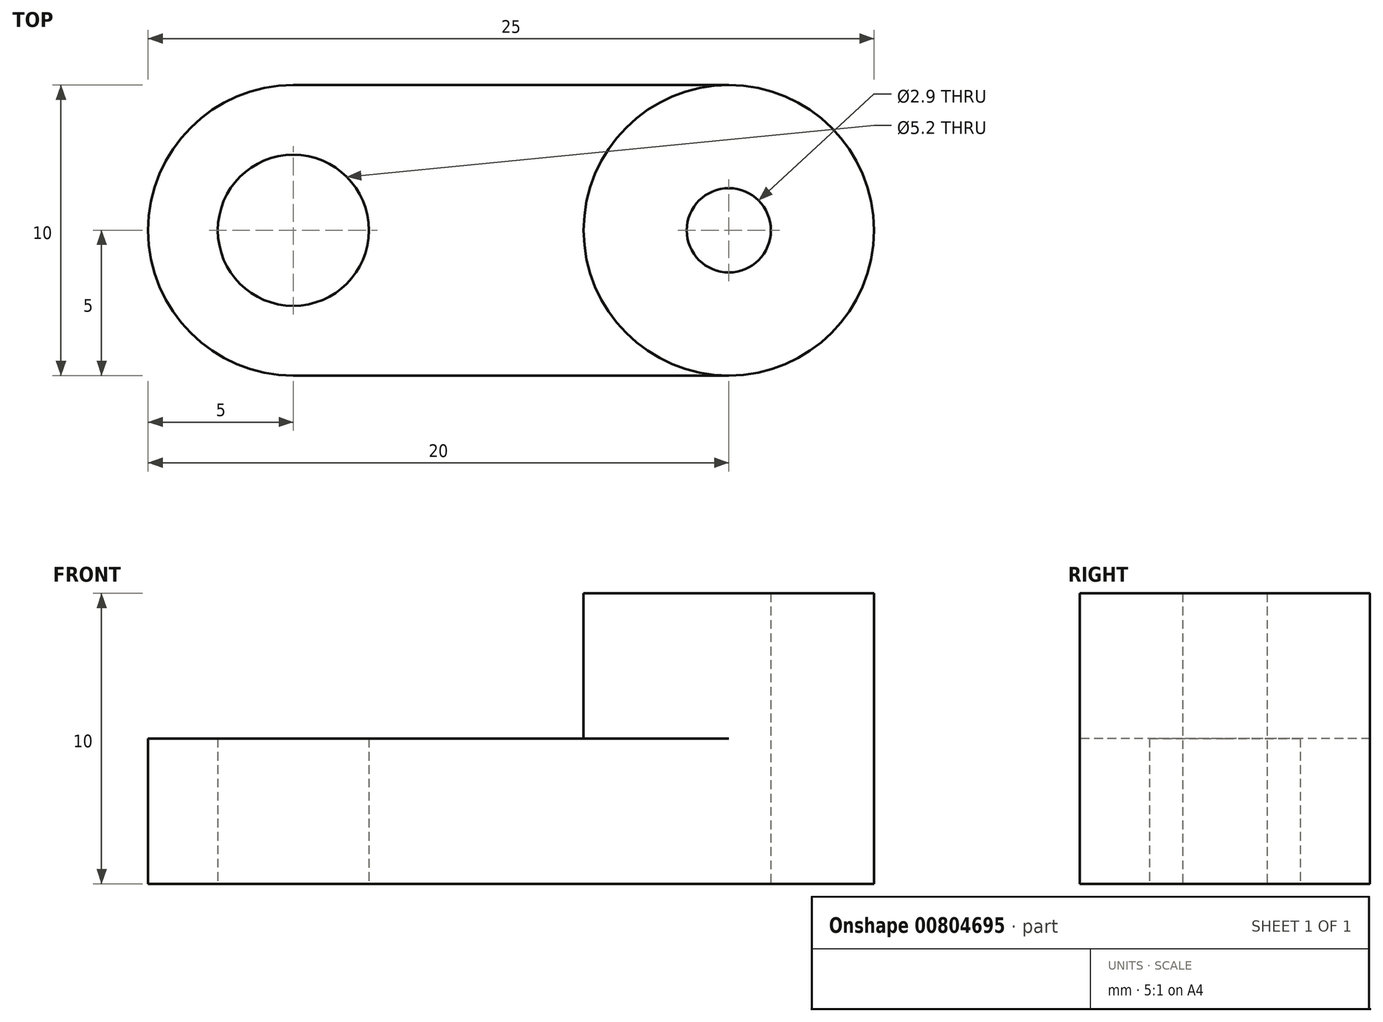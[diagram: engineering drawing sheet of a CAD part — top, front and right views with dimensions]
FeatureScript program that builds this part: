
annotation { "Feature Type Name" : "Feature", "Feature Type Description" : "" }
export const myFeature = defineFeature(function(context is Context, id is Id, definition is map)
    precondition{}
    {
        {
            var Q0;
            Q0=qCreatedBy(makeId("Top.planeOp"),FACE);
            var sketch = newSketch(context, id + "F0", { "sketchPlane" : qUnion([Q0])});
            skLineSegment(sketch, "E0", {"start": v(0, 0) * mm, "end": v(15, 0) * mm});
            skArc(sketch, "E1.0.startCap", {"start": v(0, -5) * mm, "mid": v(-5, 0) * mm, "end": v(0, 5) * mm});
            skArc(sketch, "E1.0.endCap", {"start": v(15, 5) * mm, "mid": v(20, 0) * mm, "end": v(15, -5) * mm});
            skLineSegment(sketch, "E1.0.left", {"start": v(0, 5) * mm, "end": v(15, 5) * mm});
            skLineSegment(sketch, "E1.0.right", {"start": v(0, -5) * mm, "end": v(15, -5) * mm});
            skCircle(sketch, "E2", {"center": v(0, 0) * mm, "radius": 2.6 * mm});
            skCircle(sketch, "E3", {"center": v(15, 0) * mm, "radius": 1.45 * mm});
            skSolve(sketch);
        }
        {
            var Q0;
            Q0=qSketchRegion(id+"F0",true);
            extrude(context, id + "F1", {"entities" : qUnion([Q0]), "depth" : 5 * mm, "offsetDistance" : 25 * mm});
        }
        {
            var Q0;
            Q0=makeQuery(id+"F1.opExtrude","CAP_FACE",FACE,{"disambiguationData":[OSD([sQuery(id+"F0.wireOp",EDGE,"E1.0.startCap"),sQuery(id+"F0.wireOp",EDGE,"E1.0.endCap"),sQuery(id+"F0.wireOp",EDGE,"E1.0.left"),sQuery(id+"F0.wireOp",EDGE,"E1.0.right"),sQuery(id+"F0.wireOp",EDGE,"E2"),sQuery(id+"F0.wireOp",EDGE,"E3")])],"isStart":false});
            var sketch = newSketch(context, id + "F2", { "sketchPlane" : qUnion([Q0])});
            skCircle(sketch, "E4.0", {"center": v(15, 0) * mm, "radius": 1.45 * mm});
            skCircle(sketch, "E5", {"center": v(15, 0) * mm, "radius": 5 * mm});
            skSolve(sketch);
        }
        {
            var Q0;
            Q0=qSketchRegion(id+"F2",true);
            extrude(context, id + "F3", {"entities" : qUnion([Q0]), "operationType" : NewBodyOperationType.ADD, "depth" : 5 * mm, "offsetDistance" : 25 * mm});
        }
    });
